# Revit family: 1STERN_HAND_DRYER_TUBULAR_HD
name_source: partatom
category: Generic Models
revit_build: Autodesk Revit 2017 (Build: 20160225_1515(x64)
units: mm (PartAtom-declared; Revit-internal decimal feet)

## family parameters
Can host rebar = No
Cut with Voids When Loaded = No
Host = Face
Part Type = Normal
Room Calculation Point = Yes
Round Connector Dimension = Use Diameter
Shared = No

## types (1)
- TUBULAR_HD
    AVAILABLE FINISHES = Brushed Nickel - Matt Black - Satin Gold - PVD Antique Bronze - PVD rose Gold - PVD Copper - AISI316 Material
    BADGE = https://bim.archiproducts.com
    DEPTH = 60 mm  [stored 0.19685 ft]
    DRIP PROOF = IP21
    Default Elevation = 1219 mm
    Description = TUBULAR HD - Touch-free electronic hand dryer for wall-mounted installations.‎ Concealed installation in dry walls.‎ Powered by 110V-120/220V-240Vac.‎ Hand dryer will automatically shut off after being used for more than 60 seconds.‎ Sensor settings can be customized by remote control.‎
    FINISHING MATERIAL = Chrome - Stern
    HEATER THERMAL PROTECTION = Auto resetting thermostat turns unit off at 85°C (185°F). Thermal fuse cuts unit at 142°V (288°F)
    HEIGHT = 205 mm  [stored 0.672572 ft]
    INSTALLATION = Wall mounted
    MATERIAL DESCRIPTION = Finish: Chrome
    MOTOR THERMAL PROTECTION = Auto resetting thermostat turns unit off, 120V at 135°C (257°F), 24°V at 95°C (203°F)
    Manufacturer = Stern Engineering
    Model = Tubular HD
    OPTIONS = Remote control (code 07100014), Matching battery-powered faucet (code 350400), Matching transformer-powered soap dispenser (code 350927)
    POWER SUPPLY = 110V / 120-220V / 240VA, 50-60Hz, 1.3-1.6kW
    PRODUCT CODE = 350030
    PRODUCT SHEET = https://www.archiproducts.com
    SECURITY TIME = 60 seconds auto shut off.
    SENSING RANGE = 170 ± 20 mm , self adjusting.
    STANDBY POWER = 0 W
    TECHNICAL SHEET = http://www.sternfaucets.com
    Type Comments = Concealed installation in dry walls.
    URL = http://www.sternfaucets.com
    VOLTAGE = 110 V
    WIDTH = 60 mm  [stored 0.19685 ft]

note: [stored X ft] marks values corroborated as IEEE doubles in the binary element streams (Revit-internal decimal feet)

## geometry (parser evidence)
native form markers: Sweep x2
no freeform markers — native parametric forms only
